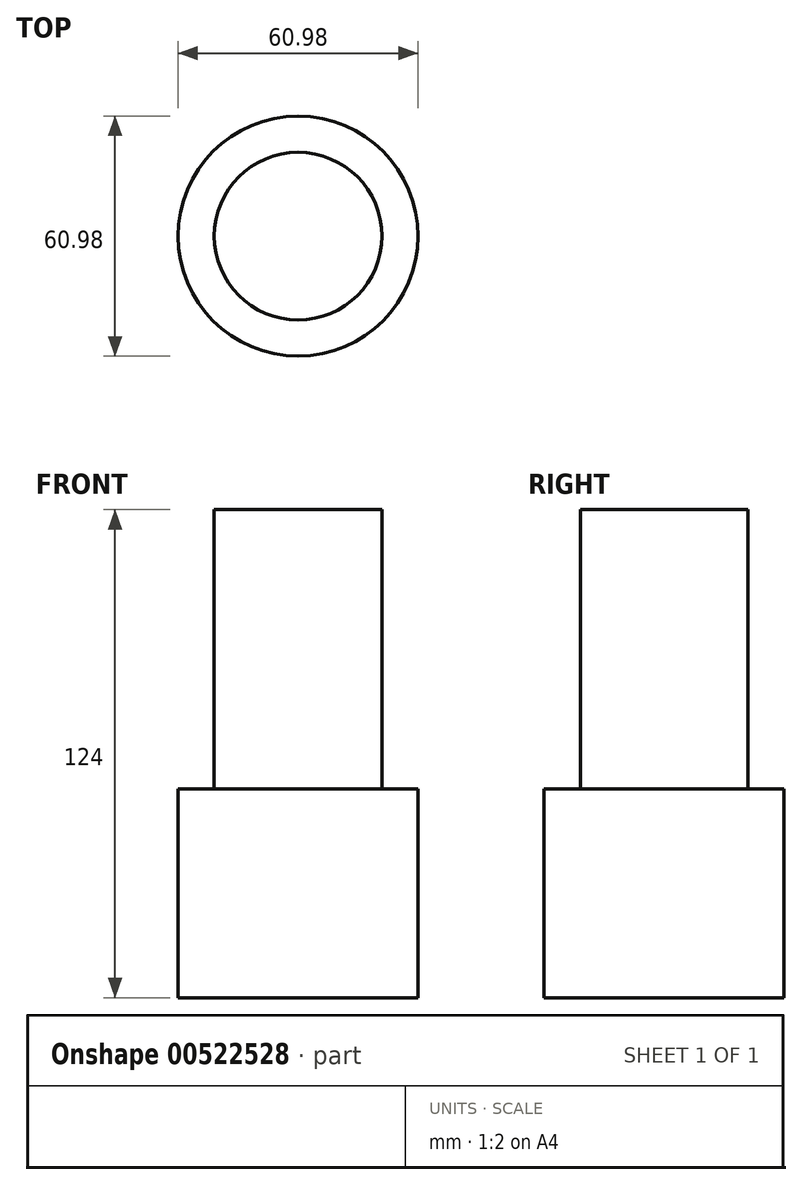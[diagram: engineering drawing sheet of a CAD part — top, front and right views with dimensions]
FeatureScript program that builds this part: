
annotation { "Feature Type Name" : "Feature", "Feature Type Description" : "" }
export const myFeature = defineFeature(function(context is Context, id is Id, definition is map)
    precondition{}
    {
        {
            var Q0;
            Q0=qCreatedBy(makeId("Top.planeOp"),FACE);
            var sketch = newSketch(context, id + "F0", { "sketchPlane" : qUnion([Q0])});
            skCircle(sketch, "E0", {"center": v(0, 0) * mm, "radius": 30.49 * mm});
            skSolve(sketch);
        }
        {
            var Q0;
            Q0 = qSketchRegion(id + "F0", true);
            extrude(context, id + "F1", {"entities" : qUnion([Q0]), "oppositeDirection" : true, "depth" : 53 * mm, "offsetDistance" : 25 * mm});
        }
        {
            var Q0;
            Q0=makeQuery(id+"F1.opExtrude","CAP_FACE",FACE,{"disambiguationData":[OSD([sQuery(id+"F0.wireOp",EDGE,"E0")])],"isStart":true});
            var sketch = newSketch(context, id + "F2", { "sketchPlane" : qUnion([Q0])});
            skCircle(sketch, "E1", {"center": v(0, 0) * mm, "radius": 21.3 * mm});
            skSolve(sketch);
        }
        {
            var Q0;
            Q0 = qSketchRegion(id + "F2", true);
            extrude(context, id + "F3", {"entities" : qUnion([Q0]), "depth" : 71 * mm, "offsetDistance" : 25 * mm});
        }
    });
